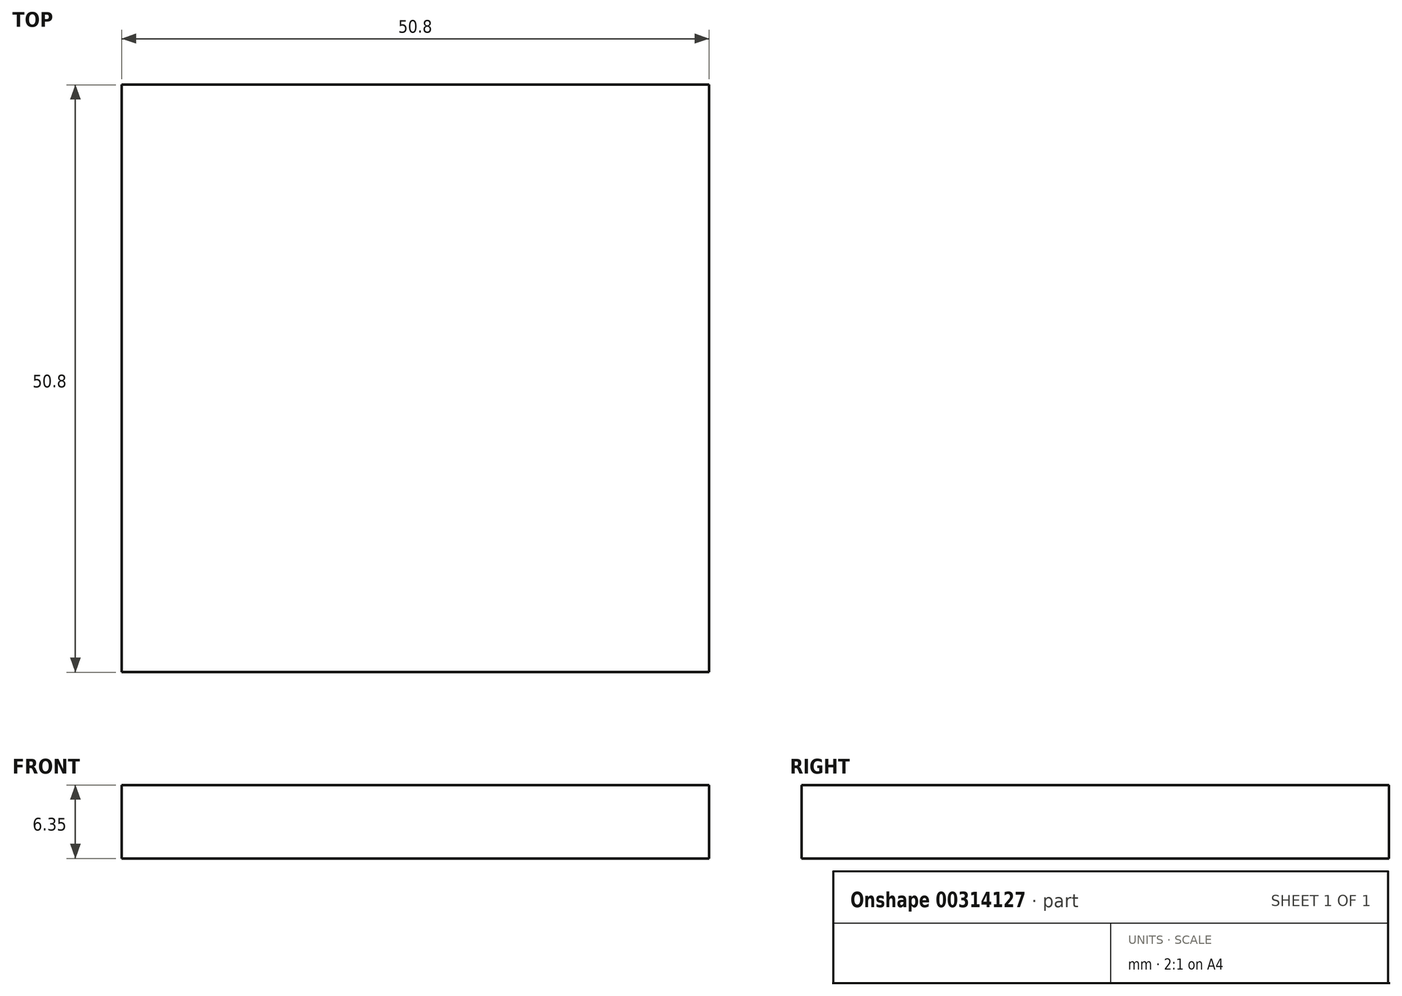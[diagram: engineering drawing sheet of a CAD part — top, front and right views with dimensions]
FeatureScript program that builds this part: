
annotation { "Feature Type Name" : "Feature", "Feature Type Description" : "" }
export const myFeature = defineFeature(function(context is Context, id is Id, definition is map)
    precondition{}
    {
        {
            var Q0;
            Q0=qCreatedBy(makeId("Top.planeOp"),FACE);
            var sketch = newSketch(context, id + "F0", { "sketchPlane" : qUnion([Q0])});
            skLineSegment(sketch, "E0.bottom", {"start": v(0, 1.3) * mm, "end": v(50.8, 1.3) * mm});
            skLineSegment(sketch, "E0.top", {"start": v(0, 52.1) * mm, "end": v(50.8, 52.1) * mm});
            skLineSegment(sketch, "E0.left", {"start": v(0, 1.3) * mm, "end": v(0, 52.1) * mm});
            skLineSegment(sketch, "E0.right", {"start": v(50.8, 1.3) * mm, "end": v(50.8, 52.1) * mm});
            skSolve(sketch);
        }
        {
            var Q0;
            Q0=makeQuery(id+"F0.imprint","IMPRINT",FACE,{"disambiguationData":[TD([[makeQuery(id+"F0.imprint","IMPRINT",EDGE,{"derivedFrom":sQuery(id+"F0.wireOp",EDGE,"E0.bottom")}),1.0]])]});
            extrude(context, id + "F1", {"entities" : qUnion([Q0]), "depth" : 6.35 * mm});
        }
    });
